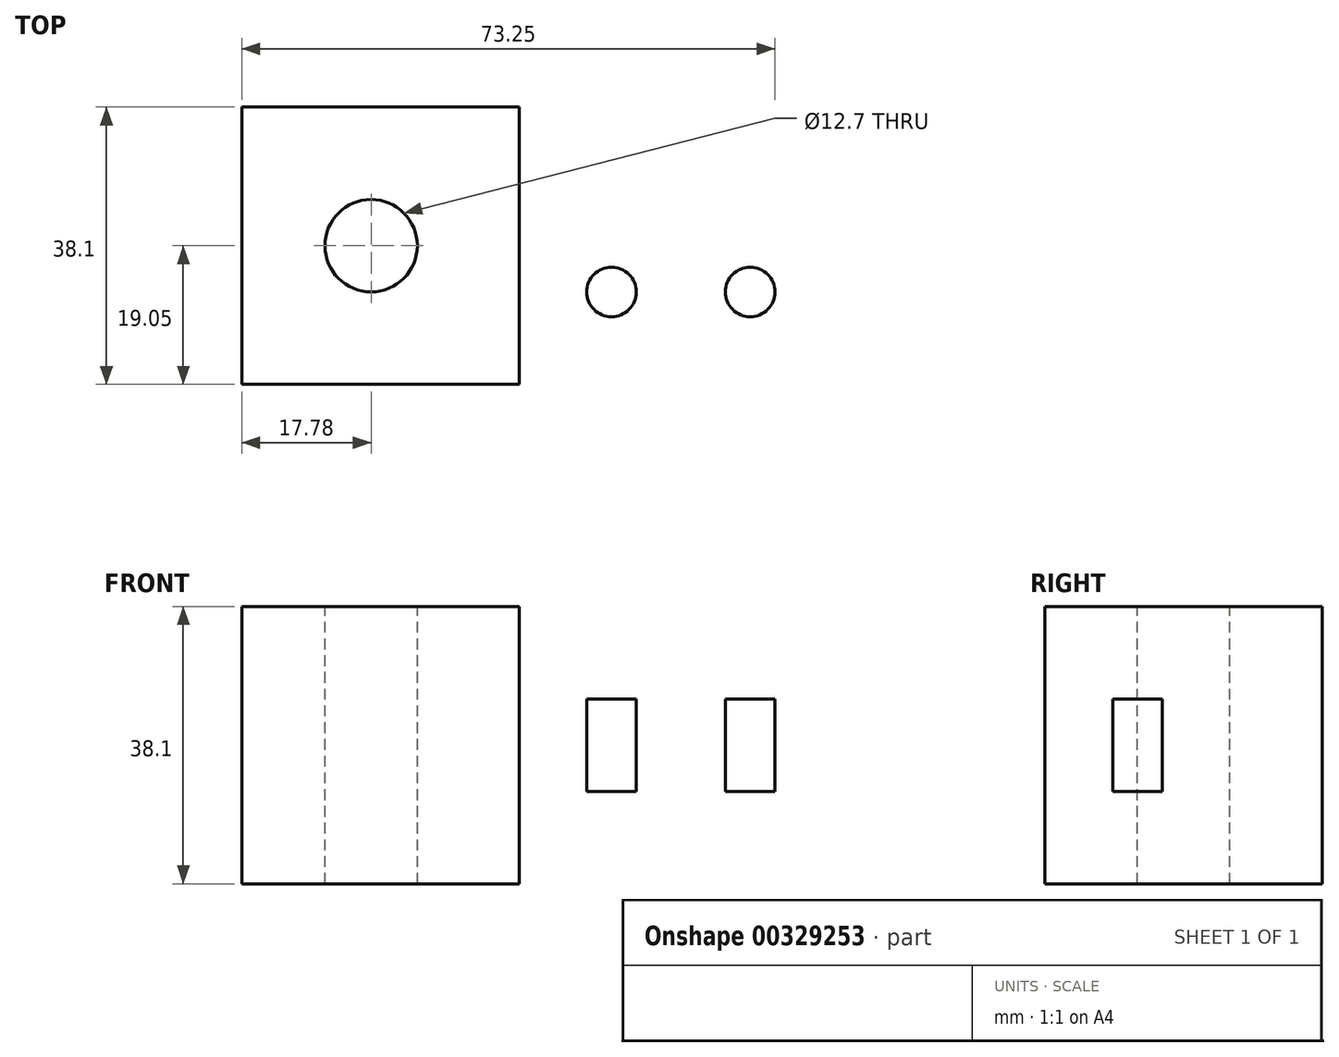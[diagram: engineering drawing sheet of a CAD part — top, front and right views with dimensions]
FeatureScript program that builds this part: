
annotation { "Feature Type Name" : "Feature", "Feature Type Description" : "" }
export const myFeature = defineFeature(function(context is Context, id is Id, definition is map)
    precondition{}
    {
        {
            var Q0;
            Q0=qCreatedBy(makeId("Front.planeOp"),FACE);
            var sketch = newSketch(context, id + "F0", { "sketchPlane" : qUnion([Q0])});
            skLineSegment(sketch, "E0", {"start": v(0, 0) * mm, "end": v(0, 38.1) * mm});
            skLineSegment(sketch, "E1", {"start": v(0, 38.1) * mm, "end": v(38.1, 38.1) * mm});
            skLineSegment(sketch, "E2", {"start": v(0, 0) * mm, "end": v(38.1, 0) * mm});
            skLineSegment(sketch, "E3", {"start": v(38.1, 0) * mm, "end": v(38.1, 12.7) * mm});
            skLineSegment(sketch, "E4", {"start": v(38.1, 12.7) * mm, "end": v(88.9, 12.7) * mm});
            skLineSegment(sketch, "E5", {"start": v(88.9, 12.7) * mm, "end": v(88.9, 25.4) * mm});
            skLineSegment(sketch, "E6", {"start": v(88.9, 25.4) * mm, "end": v(38.1, 25.4) * mm});
            skLineSegment(sketch, "E7", {"start": v(38.1, 25.4) * mm, "end": v(38.1, 38.1) * mm});
            skSolve(sketch);
        }
        {
            var Q0;
            Q0 = qSketchRegion(id + "F0", true);
            extrude(context, id + "F1", {"entities" : qUnion([Q0]), "endBound" : BoundingType.SYMMETRIC, "depth" : 38.1 * mm});
        }
        {
            var Q0;
            Q0=makeQuery(id+"F1.opExtrude","SWEPT_FACE",FACE,{"disambiguationData":[OSD([sQuery(id+"F0.wireOp",EDGE,"E6")])]});
            var sketch = newSketch(context, id + "F2", { "sketchPlane" : qUnion([Q0])});
            skLineSegment(sketch, "E8", {"start": v(38.1, 19.05) * mm, "end": v(38.1, -19.05) * mm});
            skLineSegment(sketch, "E9", {"start": v(38.1, -19.05) * mm, "end": v(69.85, -19.05) * mm});
            skLineSegment(sketch, "E10", {"start": v(38.1, 19.05) * mm, "end": v(69.85, 19.05) * mm});
            skArc(sketch, "E11", {"start": v(69.85, -19.05) * mm, "mid": v(88.9, 0) * mm, "end": v(69.85, 19.05) * mm});
            skSolve(sketch);
        }
        {
            var Q0;
            {var subQ0=sQuery(id+"F2.wireOp",EDGE,"E11");var subQ1=sQuery(id+"F0.wireOp",EDGE,"E6");var subQ2=makeQuery(id+"F1.opExtrude","CAP_EDGE",EDGE,{"disambiguationData":[OSD([subQ1])],"isStart":true});var subQ3=makeQuery(id+"F2.imprint","INTERSECT",VERTEX,{"derivedFrom":[subQ2,sQuery(id+"F2.wireOp",EDGE,"E10"),subQ0]});Q0=makeQuery(id+"F2.imprint","IMPRINT",FACE,{"disambiguationData":[TD([[makeQuery(id+"F2.imprint","IMPRINT",EDGE,{"disambiguationData":[TD([[subQ3,1.0]])],"derivedFrom":subQ0}),-1.0]])]});}
            var Q1;
            {var subQ0=sQuery(id+"F2.wireOp",EDGE,"E11");var subQ1=sQuery(id+"F0.wireOp",EDGE,"E6");var subQ2=makeQuery(id+"F1.opExtrude","CAP_EDGE",EDGE,{"disambiguationData":[OSD([subQ1])],"isStart":false});var subQ3=makeQuery(id+"F2.imprint","INTERSECT",VERTEX,{"derivedFrom":[subQ2,sQuery(id+"F2.wireOp",EDGE,"E9"),subQ0]});Q1=makeQuery(id+"F2.imprint","IMPRINT",FACE,{"disambiguationData":[TD([[makeQuery(id+"F2.imprint","IMPRINT",EDGE,{"disambiguationData":[TD([[subQ3,-1.0]])],"derivedFrom":subQ0}),-1.0]])]});}
            extrude(context, id + "F3", {"entities" : qUnion([Q0, Q1]), "operationType" : NewBodyOperationType.REMOVE, "endBound" : BoundingType.THROUGH_ALL, "oppositeDirection" : true, "depth" : 25.4 * mm});
        }
        {
            var Q0;
            Q0=makeQuery(id+"F1.opExtrude","SWEPT_FACE",FACE,{"disambiguationData":[OSD([sQuery(id+"F0.wireOp",EDGE,"E1")])]});
            var sketch = newSketch(context, id + "F4", { "sketchPlane" : qUnion([Q0])});
            skCircle(sketch, "E12", {"center": v(17.78, 0) * mm, "radius": 6.35 * mm});
            skSolve(sketch);
        }
        {
            var Q0;
            Q0=makeQuery(id+"F4.imprint","IMPRINT",FACE,{"disambiguationData":[TD([[makeQuery(id+"F4.imprint","IMPRINT",EDGE,{"derivedFrom":sQuery(id+"F4.wireOp",EDGE,"E12")}),1.0]])]});
            extrude(context, id + "F5", {"entities" : qUnion([Q0]), "operationType" : NewBodyOperationType.REMOVE, "endBound" : BoundingType.THROUGH_ALL, "oppositeDirection" : true, "depth" : 25.4 * mm});
        }
        {
            var Q0;
            Q0=makeQuery(id+"F1.opExtrude","SWEPT_FACE",FACE,{"disambiguationData":[OSD([sQuery(id+"F0.wireOp",EDGE,"E6")])]});
            var sketch = newSketch(context, id + "F6", { "sketchPlane" : qUnion([Q0])});
            skLineSegment(sketch, "E13", {"start": v(29.46, 0) * mm, "end": v(90.95, 0) * mm, "construction": true});
            skPoint(sketch, "E13.endSnap0", {"position": v(88.9, 0) * mm});
            skCircle(sketch, "E14", {"center": v(50.8, 6.35) * mm, "radius": 3.4 * mm});
            skCircle(sketch, "E15", {"center": v(69.85, 6.35) * mm, "radius": 3.4 * mm});
            skCircle(sketch, "E16.MirrorC", {"center": v(50.8, -6.35) * mm, "radius": 3.4 * mm});
            skCircle(sketch, "E17.MirrorC", {"center": v(69.85, -6.35) * mm, "radius": 3.4 * mm});
            skSolve(sketch);
        }
        {
            var Q0;
            Q0=makeQuery(id+"F6.imprint","IMPRINT",FACE,{"disambiguationData":[TD([[makeQuery(id+"F6.imprint","IMPRINT",EDGE,{"derivedFrom":sQuery(id+"F6.wireOp",EDGE,"E14")}),1.0]])]});
            var Q1;
            Q1=makeQuery(id+"F6.imprint","IMPRINT",FACE,{"disambiguationData":[TD([[makeQuery(id+"F6.imprint","IMPRINT",EDGE,{"derivedFrom":sQuery(id+"F6.wireOp",EDGE,"E15")}),1.0]])]});
            var Q2;
            Q2=makeQuery(id+"F6.imprint","IMPRINT",FACE,{"disambiguationData":[TD([[makeQuery(id+"F6.imprint","IMPRINT",EDGE,{"derivedFrom":sQuery(id+"F6.wireOp",EDGE,"E17.MirrorC")}),-1.0]])]});
            var Q3;
            Q3=makeQuery(id+"F6.imprint","IMPRINT",FACE,{"disambiguationData":[TD([[makeQuery(id+"F6.imprint","IMPRINT",EDGE,{"derivedFrom":sQuery(id+"F6.wireOp",EDGE,"E16.MirrorC")}),-1.0]])]});
            var Q4;
            Q4=sQuery(id+"F6.wireOp",EDGE,"E14");
            var Q5;
            Q5=sQuery(id+"F6.wireOp",EDGE,"E15");
            var Q6;
            Q6=sQuery(id+"F6.wireOp",EDGE,"E17.MirrorC");
            var Q7;
            Q7=sQuery(id+"F6.wireOp",EDGE,"E16.MirrorC");
            extrude(context, id + "F7", {"entities" : qUnion([Q0, Q1, Q2, Q3]), "operationType" : NewBodyOperationType.REMOVE, "surfaceEntities" : qUnion([Q4, Q5, Q6, Q7]), "endBound" : BoundingType.THROUGH_ALL, "oppositeDirection" : true, "depth" : 25.4 * mm});
        }
    });
